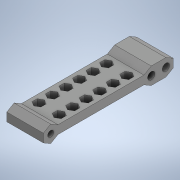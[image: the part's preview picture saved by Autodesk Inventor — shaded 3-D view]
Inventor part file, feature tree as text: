
AUTODESK INVENTOR PART (.ipt)
format: ipt  version: 2020 (Build 240168000, 168)  size: 385,024 bytes
history: native  units: in
note: dims shown in document units (in); Inventor stores cm internally (conversion verified against a paired STEP export)
features: sketch x6, extrude x5, projected_geometry x3, plane x2, mirror x1
ambient origin geometry x8: Origin, YZ Plane, XZ Plane, XY Plane, X Axis, Y Axis, Z Axis, Center Point
bodies: Solid1 (feature_tree)
feature tree (17):
  extrude  "Extrusion1"  Depth=2.7957in
  plane  "Work Plane1"
  extrude  "Extrusion2"  Depth=0.7874in
  sketch  "Sketch4"  dims[d4=0.0in d5=0.0827in]
  extrude  "Extrusion4"  Depth=0.0827in
  plane  "Work Plane2"
  extrude  "Extrusion6"  Depth=2.4807in
  mirror  "Mirror2"
  extrude  "Extrusion7"  Depth=0.315in
  sketch  "Sketch1"  dims[d0=0.1818in d1=2.7957in]
  sketch  "Sketch2"  dims[d2=0.1299in d3=0.7874in]
  sketch  "Sketch5"  dims[d6=0.7874in d7=0.0in d28=2.4807in]
  sketch  "Sketch7"  dims[d29=0.315in d31=0.315in]
  projected_geometry  "Projected Loop7"
  projected_geometry  "Projected Loop8"
  sketch  "Sketch8"  dims[d33=0.1575in d34=0.2362in d35=0.0in d38=0.315in d39=0.2756in d40=-0.3092in d41=0.0787in d42=0.0787in d43=0.0787in d44=2.3622in d46=0.2913in d47=0.3937in d49=0.3937in d51=2.3622in d53=0.2913in d54=0.3937in d56=0.3937in d58=0.0in d59=0.0in]
  projected_geometry  "Projected Loop9"
